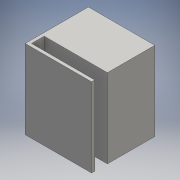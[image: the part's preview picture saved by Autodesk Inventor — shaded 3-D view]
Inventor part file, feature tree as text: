
AUTODESK INVENTOR PART (.ipt)
format: ipt  version: 2016 (Build 200138000, 138)  size: 86,528 bytes
history: native  units: mm
features: extrude x1, sketch x1
ambient origin geometry x8: Origin, YZ Plane, XZ Plane, XY Plane, X Axis, Y Axis, Z Axis, Center Point
bodies: Solid1 (feature_tree)
feature tree (2):
  extrude  "Extrusion1"  Depth=40.0mm
  sketch  "Sketch1"  dims[d0=42.0mm d1=40.0mm d2=30.0mm d3=50.0mm d4=0.0mm]
